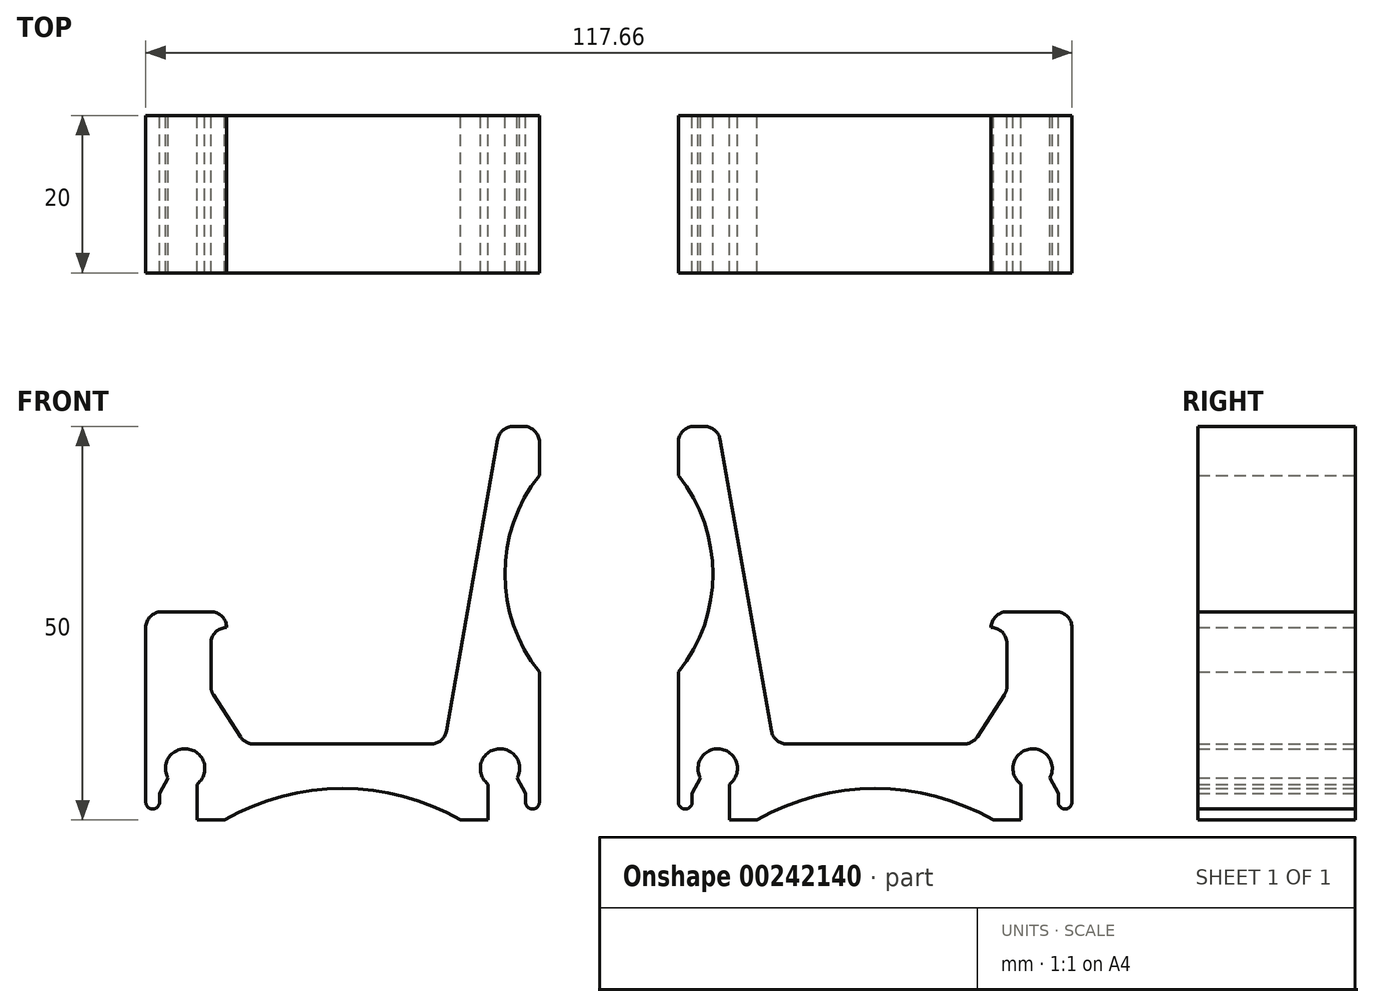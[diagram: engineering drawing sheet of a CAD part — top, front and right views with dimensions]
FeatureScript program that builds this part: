
annotation { "Feature Type Name" : "Feature", "Feature Type Description" : "" }
export const myFeature = defineFeature(function(context is Context, id is Id, definition is map)
    precondition{}
    {
        {
            var Q0;
            Q0=qCreatedBy(makeId("Front.planeOp"),FACE);
            var sketch = newSketch(context, id + "F0", { "sketchPlane" : qUnion([Q0])});
            skLineSegment(sketch, "E0", {"start": v(-40.32, 16.8) * mm, "end": v(-46.6, 16.8) * mm});
            skLineSegment(sketch, "E1", {"start": v(-48.6, 14.8) * mm, "end": v(-48.6, -7.38) * mm});
            skLineSegment(sketch, "E2", {"start": v(-45.1, -9.65) * mm, "end": v(-38.6, -9.65) * mm});
            skArc(sketch, "E3", {"start": v(-42.1, -5.1) * mm, "mid": v(-43.6, -0.6) * mm, "end": v(-45.1, -5.1) * mm});
            skPoint(sketch, "E3.centerSnap0", {"position": v(-43.6, -9.65) * mm});
            skPoint(sketch, "E4", {"position": v(-43.6, -5.6) * mm});
            skLineSegment(sketch, "E5", {"start": v(-45.1, -5.1) * mm, "end": v(-45.1, -9.65) * mm});
            skLineSegment(sketch, "E6", {"start": v(-42.1, -5.1) * mm, "end": v(-42.1, -9.65) * mm});
            skLineSegment(sketch, "E7", {"start": v(-45.1, -9.65) * mm, "end": v(-42.1, -9.65) * mm});
            skLineSegment(sketch, "E8", {"start": v(-8.6, -9.65) * mm, "end": v(-2.1, -9.65) * mm});
            skLineSegment(sketch, "E9", {"start": v(1.4, -7.65) * mm, "end": v(1.4, -5.02) * mm});
            skLineSegment(sketch, "E10", {"start": v(-0.6, 40.35) * mm, "end": v(-1.92, 40.35) * mm});
            skLineSegment(sketch, "E11", {"start": v(-12.39, 0) * mm, "end": v(-34.88, 0) * mm});
            skLineSegment(sketch, "E12", {"start": v(-38.32, 14.8) * mm, "end": v(-38.32, 14.8) * mm});
            skLineSegment(sketch, "E13", {"start": v(-36.56, 0.91) * mm, "end": v(-40, 6.22) * mm});
            skLineSegment(sketch, "E14", {"start": v(-40.32, 7.3) * mm, "end": v(-40.32, 12.8) * mm});
            skLineSegment(sketch, "E15", {"start": v(-3.89, 38.7) * mm, "end": v(-10.42, 1.65) * mm});
            skPoint(sketch, "E16.orphan", {"position": v(-2.69, 0) * mm});
            skLineSegment(sketch, "E17", {"start": v(-48.6, -3.1) * mm, "end": v(-46.1, -3.1) * mm, "construction": true});
            skLineSegment(sketch, "E18", {"start": v(1.4, -5.02) * mm, "end": v(-23.6, -5.02) * mm, "construction": true});
            skArc(sketch, "E19.MirrorCS", {"start": v(-5.1, -5.1) * mm, "mid": v(-3.6, -0.6) * mm, "end": v(-2.1, -5.1) * mm});
            skLineSegment(sketch, "E20.MirrorCS", {"start": v(-5.1, -5.1) * mm, "end": v(-5.1, -9.65) * mm});
            skLineSegment(sketch, "E21.MirrorCS", {"start": v(-2.1, -5.1) * mm, "end": v(-2.1, -9.65) * mm});
            skLineSegment(sketch, "E22.MirrorCS", {"start": v(-2.1, -9.65) * mm, "end": v(-5.1, -9.65) * mm});
            skPoint(sketch, "E23.visualSharp", {"position": v(-3.6, 40.35) * mm});
            skArc(sketch, "E23.filletArc", {"start": v(-1.92, 40.35) * mm, "mid": v(-3.2, 39.88) * mm, "end": v(-3.89, 38.7) * mm});
            skPoint(sketch, "E24.visualSharp", {"position": v(1.4, 40.35) * mm});
            skArc(sketch, "E24.filletArc", {"start": v(1.4, 38.35) * mm, "mid": v(0.82, 39.76) * mm, "end": v(-0.6, 40.35) * mm});
            skPoint(sketch, "E25.visualSharp", {"position": v(-38.32, 16.8) * mm});
            skArc(sketch, "E25.filletArc", {"start": v(-38.32, 14.8) * mm, "mid": v(-38.91, 16.21) * mm, "end": v(-40.32, 16.8) * mm});
            skArc(sketch, "E26.filletArc", {"start": v(-38.32, 14.8) * mm, "mid": v(-39.74, 14.21) * mm, "end": v(-40.32, 12.8) * mm});
            skPoint(sketch, "E27.visualSharp", {"position": v(-40.32, 6.71) * mm});
            skArc(sketch, "E27.filletArc", {"start": v(-40.32, 7.3) * mm, "mid": v(-40.24, 6.74) * mm, "end": v(-40, 6.22) * mm});
            skPoint(sketch, "E28.visualSharp", {"position": v(-48.6, 16.8) * mm});
            skArc(sketch, "E28.filletArc", {"start": v(-46.6, 16.8) * mm, "mid": v(-48.01, 16.21) * mm, "end": v(-48.6, 14.8) * mm});
            skPoint(sketch, "E29.visualSharp", {"position": v(-10.71, 0) * mm});
            skArc(sketch, "E29.filletArc", {"start": v(-12.39, 0) * mm, "mid": v(-11.1, 0.47) * mm, "end": v(-10.42, 1.65) * mm});
            skPoint(sketch, "E30.visualSharp", {"position": v(-35.97, 0) * mm});
            skArc(sketch, "E30.filletArc", {"start": v(-36.56, 0.91) * mm, "mid": v(-35.84, 0.24) * mm, "end": v(-34.88, 0) * mm});
            skPoint(sketch, "E31.visualSharp", {"position": v(-48.6, -9.65) * mm});
            skPoint(sketch, "E32.visualSharp", {"position": v(1.4, -9.65) * mm});
            skLineSegment(sketch, "E33", {"start": v(10.23, 41.43) * mm, "end": v(10.23, -9.58) * mm, "construction": true});
            skLineSegment(sketch, "E34.MirrorCS", {"start": v(58.79, 14.8) * mm, "end": v(58.79, 14.8) * mm});
            skArc(sketch, "E35.MirrorCS", {"start": v(60.79, 7.3) * mm, "mid": v(60.7, 6.74) * mm, "end": v(60.46, 6.22) * mm});
            skArc(sketch, "E36.MirrorCS", {"start": v(57.02, 0.91) * mm, "mid": v(56.3, 0.24) * mm, "end": v(55.35, 0) * mm});
            skArc(sketch, "E37.MirrorCS", {"start": v(58.79, 14.8) * mm, "mid": v(60.2, 14.21) * mm, "end": v(60.79, 12.8) * mm});
            skLineSegment(sketch, "E38.MirrorCS", {"start": v(21.06, 40.35) * mm, "end": v(22.38, 40.35) * mm});
            skLineSegment(sketch, "E39.MirrorCS", {"start": v(65.56, -9.65) * mm, "end": v(62.56, -9.65) * mm});
            skArc(sketch, "E40.MirrorCS", {"start": v(67.06, 16.8) * mm, "mid": v(68.47, 16.21) * mm, "end": v(69.06, 14.8) * mm});
            skArc(sketch, "E41.MirrorCS", {"start": v(19.06, 38.35) * mm, "mid": v(19.64, 39.76) * mm, "end": v(21.06, 40.35) * mm});
            skArc(sketch, "E42.MirrorCS", {"start": v(22.38, 40.35) * mm, "mid": v(23.67, 39.88) * mm, "end": v(24.35, 38.7) * mm});
            skArc(sketch, "E43.MirrorCS", {"start": v(58.79, 14.8) * mm, "mid": v(59.37, 16.21) * mm, "end": v(60.79, 16.8) * mm});
            skArc(sketch, "E44.MirrorCS", {"start": v(32.85, 0) * mm, "mid": v(31.57, 0.47) * mm, "end": v(30.88, 1.65) * mm});
            skLineSegment(sketch, "E45.MirrorCS", {"start": v(24.35, 38.7) * mm, "end": v(30.88, 1.65) * mm});
            skPoint(sketch, "E46.MirrorP", {"position": v(64.06, -3.1) * mm});
            skArc(sketch, "E47.MirrorCS", {"start": v(62.56, -5.1) * mm, "mid": v(64.06, -0.6) * mm, "end": v(65.56, -5.1) * mm});
            skLineSegment(sketch, "E48.MirrorCS", {"start": v(25.56, -5.1) * mm, "end": v(25.56, -9.65) * mm});
            skLineSegment(sketch, "E49.MirrorCS", {"start": v(32.85, 0) * mm, "end": v(55.35, 0) * mm});
            skLineSegment(sketch, "E50.MirrorCS", {"start": v(60.79, 16.8) * mm, "end": v(67.06, 16.8) * mm});
            skPoint(sketch, "E51.MirrorP", {"position": v(23.15, 0) * mm});
            skPoint(sketch, "E52.MirrorP", {"position": v(64.06, -9.65) * mm});
            skArc(sketch, "E53.MirrorCS", {"start": v(25.56, -5.1) * mm, "mid": v(24.06, -0.6) * mm, "end": v(22.56, -5.1) * mm});
            skLineSegment(sketch, "E54.MirrorCS", {"start": v(69.06, -3.1) * mm, "end": v(64.06, -3.1) * mm, "construction": true});
            skPoint(sketch, "E55.MirrorP", {"position": v(31.17, 0) * mm});
            skLineSegment(sketch, "E56.MirrorCS", {"start": v(67.06, -9.65) * mm, "end": v(59.06, -9.65) * mm});
            skPoint(sketch, "E57.MirrorP", {"position": v(69.06, -9.65) * mm});
            skLineSegment(sketch, "E58.MirrorCS", {"start": v(57.02, 0.91) * mm, "end": v(60.46, 6.22) * mm});
            skLineSegment(sketch, "E59.MirrorCS", {"start": v(65.56, -5.1) * mm, "end": v(65.56, -9.65) * mm});
            skLineSegment(sketch, "E60.MirrorCS", {"start": v(19.06, -5.02) * mm, "end": v(44.06, -5.02) * mm, "construction": true});
            skLineSegment(sketch, "E61.MirrorCS", {"start": v(44.06, -5.02) * mm, "end": v(44.06, 0) * mm, "construction": true});
            skLineSegment(sketch, "E62.MirrorCS", {"start": v(22.56, -5.1) * mm, "end": v(22.56, -9.65) * mm});
            skLineSegment(sketch, "E63.MirrorCS", {"start": v(69.06, 14.8) * mm, "end": v(69.06, -7.65) * mm});
            skLineSegment(sketch, "E64.MirrorCS", {"start": v(22.56, -9.65) * mm, "end": v(25.56, -9.65) * mm});
            skPoint(sketch, "E65.MirrorP", {"position": v(64.06, -5.6) * mm});
            skPoint(sketch, "E66.MirrorP", {"position": v(58.79, 16.8) * mm});
            skLineSegment(sketch, "E67.MirrorCS", {"start": v(19.06, -7.65) * mm, "end": v(19.06, 9.13) * mm});
            skPoint(sketch, "E68.MirrorP", {"position": v(60.79, 6.71) * mm});
            skPoint(sketch, "E69.MirrorP", {"position": v(19.06, 40.35) * mm});
            skPoint(sketch, "E70.MirrorP", {"position": v(69.06, 16.8) * mm});
            skPoint(sketch, "E71.MirrorP", {"position": v(19.06, -9.65) * mm});
            skLineSegment(sketch, "E72.MirrorCS", {"start": v(29.06, -9.65) * mm, "end": v(21.06, -9.65) * mm});
            skPoint(sketch, "E73.MirrorP", {"position": v(56.43, 0) * mm});
            skLineSegment(sketch, "E74.MirrorCS", {"start": v(62.56, -5.1) * mm, "end": v(62.56, -9.65) * mm});
            skPoint(sketch, "E75.MirrorP", {"position": v(24.06, 40.35) * mm});
            skLineSegment(sketch, "E76.MirrorCS", {"start": v(60.79, 7.3) * mm, "end": v(60.79, 12.8) * mm});
            skLineSegment(sketch, "E77.trimOffspring", {"start": v(19.06, 34.13) * mm, "end": v(19.06, 38.35) * mm});
            skLineSegment(sketch, "E78.trimOffspring", {"start": v(1.4, 34.13) * mm, "end": v(1.4, 38.35) * mm});
            skLineSegment(sketch, "E79", {"start": v(1.4, 9.13) * mm, "end": v(1.4, -5.02) * mm});
            skArc(sketch, "E80", {"start": v(19.06, 9.13) * mm, "mid": v(23.45, 21.63) * mm, "end": v(19.06, 34.13) * mm});
            skArc(sketch, "E81.MirrorCS", {"start": v(1.4, 9.13) * mm, "mid": v(-2.98, 21.63) * mm, "end": v(1.4, 34.13) * mm});
            skArc(sketch, "E82", {"start": v(59.06, -9.65) * mm, "mid": v(44.06, -5.63) * mm, "end": v(29.06, -9.65) * mm});
            skArc(sketch, "E83.MirrorCS", {"start": v(-38.6, -9.65) * mm, "mid": v(-23.6, -5.63) * mm, "end": v(-8.6, -9.65) * mm});
            skPoint(sketch, "E84.orphan", {"position": v(-46.6, -9.65) * mm});
            skPoint(sketch, "E85.orphan", {"position": v(-48.6, -7.65) * mm});
            skPoint(sketch, "E86.end.orphan", {"position": v(-23.6, 0) * mm});
            skLineSegment(sketch, "E87", {"start": v(-23.6, -9.5) * mm, "end": v(-23.6, 4.88) * mm, "construction": true});
            skPoint(sketch, "E88.orphan", {"position": v(-0.6, -9.65) * mm});
            skPoint(sketch, "E89", {"position": v(-45.1, -7.38) * mm});
            skPoint(sketch, "E90", {"position": v(-45.1, -6.24) * mm});
            skPoint(sketch, "E91", {"position": v(-45.1, -8.51) * mm});
            skLineSegment(sketch, "E92", {"start": v(-46.85, -6.24) * mm, "end": v(-46.85, -7.38) * mm});
            skArc(sketch, "E93", {"start": v(-48.6, -7.38) * mm, "mid": v(-47.72, -8.25) * mm, "end": v(-46.85, -7.38) * mm});
            skPoint(sketch, "E94.end.orphan", {"position": v(-48.6, -6.24) * mm});
            skLineSegment(sketch, "E95", {"start": v(-46.1, -3.1) * mm, "end": v(-45.1, -3.1) * mm});
            skLineSegment(sketch, "E96", {"start": v(-45.78, -4.33) * mm, "end": v(-46.85, -6.24) * mm});
            skLineSegment(sketch, "E97.trimOffspring", {"start": v(-45.1, -3.1) * mm, "end": v(-43.6, -3.1) * mm, "construction": true});
            skLineSegment(sketch, "E98.MirrorCS", {"start": v(-1.41, -4.33) * mm, "end": v(-0.35, -6.24) * mm});
            skLineSegment(sketch, "E99.MirrorCS", {"start": v(-0.35, -6.24) * mm, "end": v(-0.35, -7.38) * mm});
            skArc(sketch, "E100.MirrorCS", {"start": v(1.4, -7.38) * mm, "mid": v(0.53, -8.25) * mm, "end": v(-0.35, -7.38) * mm});
            skPoint(sketch, "E101.orphan", {"position": v(-2.1, -7.38) * mm});
            skPoint(sketch, "E102.MirrorCS.start.orphan", {"position": v(1.4, -7.38) * mm});
            skPoint(sketch, "E103.MirrorCS.end.orphan", {"position": v(22.56, -7.38) * mm});
            skPoint(sketch, "E103.MirrorCS.start.orphan", {"position": v(19.06, -7.38) * mm});
            skArc(sketch, "E104.MirrorCS", {"start": v(19.06, -7.38) * mm, "mid": v(19.93, -8.25) * mm, "end": v(20.8, -7.38) * mm});
            skLineSegment(sketch, "E105.MirrorCS", {"start": v(20.8, -6.24) * mm, "end": v(20.8, -7.38) * mm});
            skLineSegment(sketch, "E106.MirrorCS", {"start": v(21.88, -4.33) * mm, "end": v(20.8, -6.24) * mm});
            skLineSegment(sketch, "E107.MirrorCS", {"start": v(66.24, -4.33) * mm, "end": v(67.3, -6.24) * mm});
            skArc(sketch, "E108.MirrorCS", {"start": v(69.06, -7.38) * mm, "mid": v(68.18, -8.25) * mm, "end": v(67.3, -7.38) * mm});
            skLineSegment(sketch, "E109.MirrorCS", {"start": v(67.3, -6.24) * mm, "end": v(67.3, -7.38) * mm});
            skPoint(sketch, "E110.orphan", {"position": v(65.56, -7.38) * mm});
            skPoint(sketch, "E111.MirrorCS.start.orphan", {"position": v(69.06, -7.38) * mm});
            skSolve(sketch);
        }
        {
            var Q0;
            Q0=makeQuery(id+"F0.imprint","IMPRINT",FACE,{"disambiguationData":[TD([[makeQuery(id+"F0.imprint","IMPRINT",EDGE,{"derivedFrom":sQuery(id+"F0.wireOp",EDGE,"E0")}),1.0]])]});
            var Q1;
            Q1=makeQuery(id+"F0.imprint","IMPRINT",FACE,{"disambiguationData":[TD([[makeQuery(id+"F0.imprint","IMPRINT",EDGE,{"derivedFrom":sQuery(id+"F0.wireOp",EDGE,"E34.MirrorCS")}),-1.0]])]});
            extrude(context, id + "F1", {"entities" : qUnion([Q0, Q1]), "depth" : 20 * mm});
        }
    });
